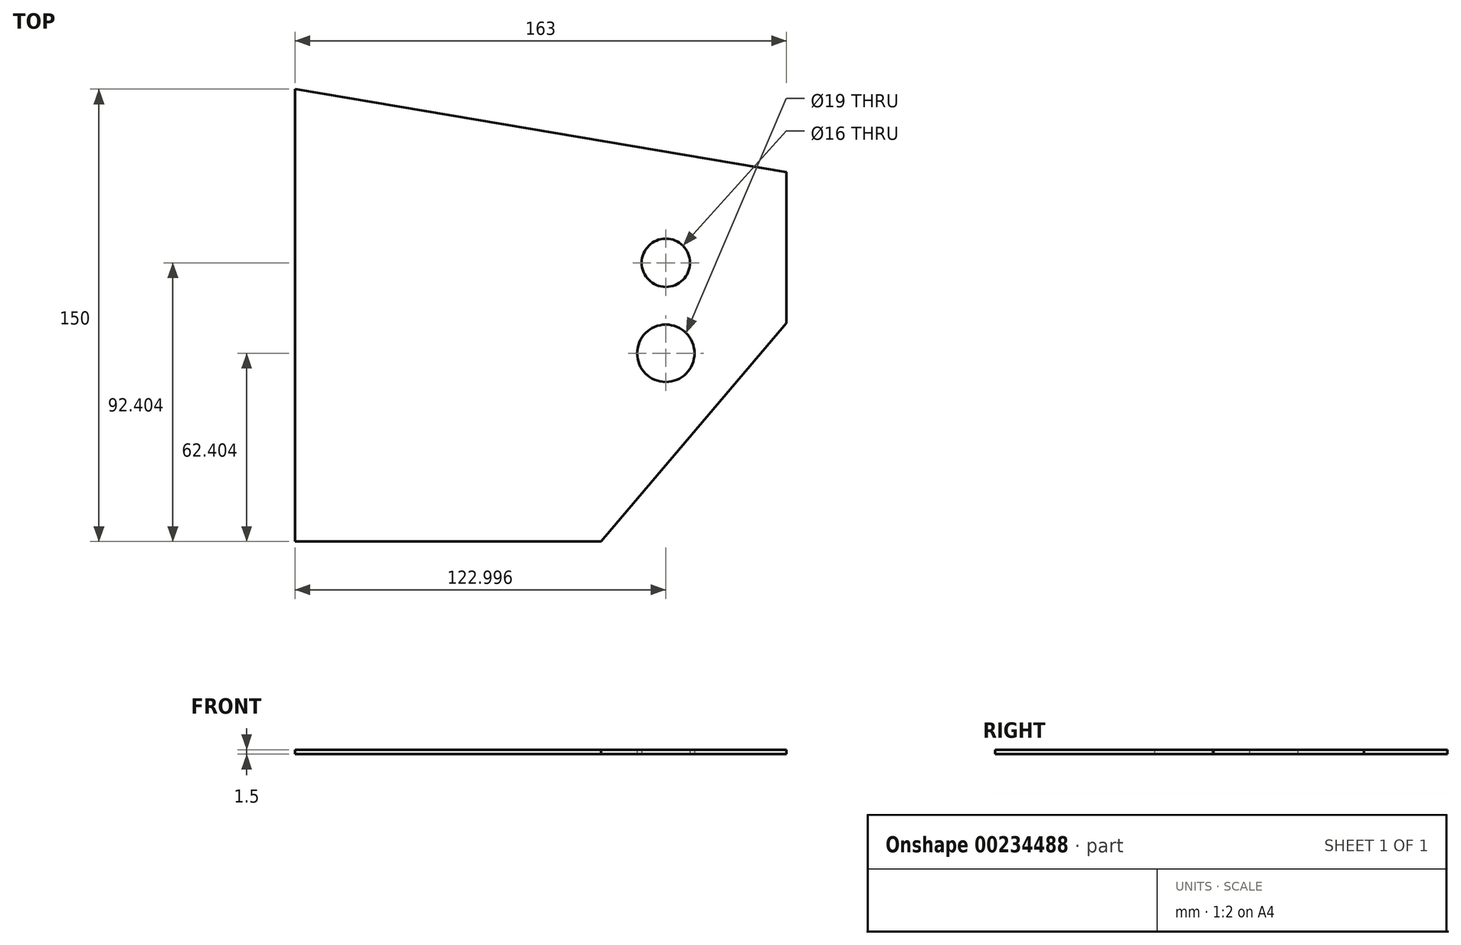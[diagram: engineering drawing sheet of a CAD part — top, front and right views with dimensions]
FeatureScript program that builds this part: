
annotation { "Feature Type Name" : "Feature", "Feature Type Description" : "" }
export const myFeature = defineFeature(function(context is Context, id is Id, definition is map)
    precondition{}
    {
        {
            var Q0;
            Q0=qCreatedBy(makeId("Top.planeOp"),FACE);
            var sketch = newSketch(context, id + "F0", { "sketchPlane" : qUnion([Q0])});
            skLineSegment(sketch, "E0.top", {"start": v(-89.22, -90.2) * mm, "end": v(12.28, -90.2) * mm});
            skLineSegment(sketch, "E0.left", {"start": v(-89.22, 59.8) * mm, "end": v(-89.22, -90.2) * mm});
            skLineSegment(sketch, "E0.right", {"start": v(73.78, 32.21) * mm, "end": v(73.78, -17.79) * mm});
            skLineSegment(sketch, "E1", {"start": v(12.28, -90.2) * mm, "end": v(73.78, -17.79) * mm});
            skLineSegment(sketch, "E2", {"start": v(73.78, -17.79) * mm, "end": v(73.78, 32.21) * mm, "construction": true});
            skLineSegment(sketch, "E3", {"start": v(-89.22, 59.8) * mm, "end": v(73.78, 32.21) * mm});
            skLineSegment(sketch, "E4", {"start": v(73.78, 32.21) * mm, "end": v(73.78, -81.79) * mm, "construction": true});
            skLineSegment(sketch, "E5", {"start": v(33.78, 38.95) * mm, "end": v(33.78, 10.21) * mm, "construction": true});
            skLineSegment(sketch, "E6", {"start": v(73.78, 32.21) * mm, "end": v(-89.22, 32.21) * mm, "construction": true});
            skLineSegment(sketch, "E7", {"start": v(73.78, 2.21) * mm, "end": v(41.78, 2.21) * mm, "construction": true});
            skLineSegment(sketch, "E8", {"start": v(-89.22, -27.79) * mm, "end": v(24.28, -27.79) * mm, "construction": true});
            skCircle(sketch, "E9", {"center": v(33.78, -27.79) * mm, "radius": 9.5 * mm});
            skCircle(sketch, "E10", {"center": v(33.78, 2.21) * mm, "radius": 8 * mm});
            skLineSegment(sketch, "E11.trimOffspring", {"start": v(33.78, -37.29) * mm, "end": v(33.78, -88.62) * mm, "construction": true});
            skLineSegment(sketch, "E12.trimOffspring", {"start": v(43.28, -27.79) * mm, "end": v(73.78, -27.79) * mm, "construction": true});
            skLineSegment(sketch, "E13.trimOffspring", {"start": v(25.78, 2.21) * mm, "end": v(-89.22, 2.21) * mm, "construction": true});
            skLineSegment(sketch, "E14.trimOffspring", {"start": v(33.78, -5.79) * mm, "end": v(33.78, -18.29) * mm, "construction": true});
            skSolve(sketch);
        }
        {
            var Q0;
            Q0=qSketchRegion(id+"F0",true);
            extrude(context, id + "F1", {"entities" : qUnion([Q0]), "depth" : 1.5 * mm});
        }
    });
